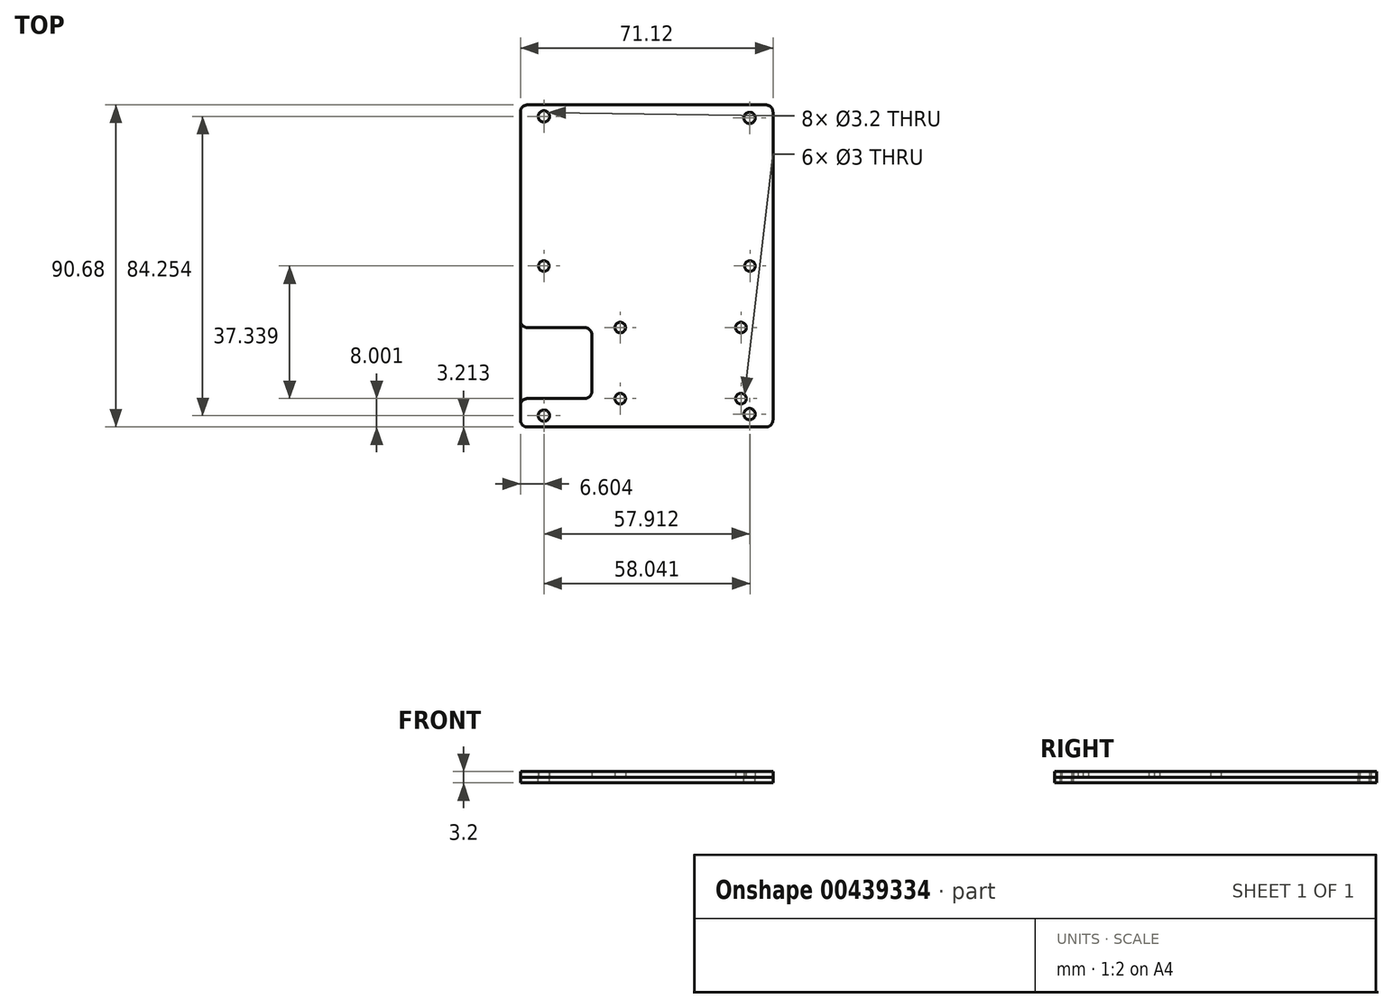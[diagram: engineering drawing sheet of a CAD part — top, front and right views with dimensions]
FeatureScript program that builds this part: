
annotation { "Feature Type Name" : "Feature", "Feature Type Description" : "" }
export const myFeature = defineFeature(function(context is Context, id is Id, definition is map)
    precondition{}
    {
        {
            var Q0;
            Q0=qCreatedBy(makeId("Top.planeOp"),FACE);
            var sketch = newSketch(context, id + "F0", { "sketchPlane" : qUnion([Q0])});
            skLineSegment(sketch, "E0.bottom", {"start": v(35.56, -55.5) * mm, "end": v(-35.56, -55.5) * mm});
            skLineSegment(sketch, "E0.top", {"start": v(35.56, 55.5) * mm, "end": v(-35.56, 55.5) * mm});
            skLineSegment(sketch, "E0.left", {"start": v(35.56, -55.5) * mm, "end": v(35.56, 55.5) * mm});
            skLineSegment(sketch, "E0.right", {"start": v(-35.56, -55.5) * mm, "end": v(-35.56, 55.5) * mm});
            skPoint(sketch, "E0.middle", {"position": v(0, 0) * mm});
            skCircle(sketch, "E1", {"center": v(-28.96, 42.13) * mm, "radius": 1.6 * mm});
            skCircle(sketch, "E2", {"center": v(28.96, 41.7) * mm, "radius": 1.6 * mm});
            skLineSegment(sketch, "E3", {"start": v(-75.95, 0) * mm, "end": v(69.97, 0) * mm, "construction": true});
            skLineSegment(sketch, "E4", {"start": v(0, -74.25) * mm, "end": v(0, 72.53) * mm, "construction": true});
            skLineSegment(sketch, "E5", {"start": v(-28.96, 42.13) * mm, "end": v(28.96, 41.7) * mm, "construction": true});
            skPoint(sketch, "E6", {"position": v(0, 41.91) * mm});
            skCircle(sketch, "E7.MirrorC", {"center": v(-28.96, -42.13) * mm, "radius": 1.6 * mm});
            skCircle(sketch, "E8.MirrorC", {"center": v(28.96, -41.7) * mm, "radius": 1.6 * mm});
            skLineSegment(sketch, "E9.bottom", {"start": v(35.56, 55.5) * mm, "end": v(16.5, 55.5) * mm});
            skLineSegment(sketch, "E9.top", {"start": v(35.56, 45.34) * mm, "end": v(22.86, 45.34) * mm});
            skLineSegment(sketch, "E9.left", {"start": v(35.56, 55.5) * mm, "end": v(35.56, 45.34) * mm});
            skLineSegment(sketch, "E9.right", {"start": v(16.5, 55.5) * mm, "end": v(16.5, 51.69) * mm});
            skPoint(sketch, "E10.visualSharp", {"position": v(16.5, 45.34) * mm});
            skArc(sketch, "E10.filletArc", {"start": v(16.5, 51.69) * mm, "mid": v(18.37, 47.2) * mm, "end": v(22.86, 45.34) * mm});
            skLineSegment(sketch, "E11.MirrorCS", {"start": v(-35.56, 45.34) * mm, "end": v(-22.86, 45.34) * mm});
            skPoint(sketch, "E12.MirrorP", {"position": v(-16.5, 45.34) * mm});
            skArc(sketch, "E13.MirrorCS", {"start": v(-16.5, 51.69) * mm, "mid": v(-18.37, 47.2) * mm, "end": v(-22.86, 45.34) * mm});
            skLineSegment(sketch, "E14.MirrorCS", {"start": v(-16.5, 55.5) * mm, "end": v(-16.5, 51.69) * mm});
            skLineSegment(sketch, "E15.MirrorCS", {"start": v(35.56, -45.34) * mm, "end": v(22.86, -45.34) * mm});
            skArc(sketch, "E16.MirrorCS", {"start": v(16.5, -51.69) * mm, "mid": v(18.37, -47.2) * mm, "end": v(22.86, -45.34) * mm});
            skLineSegment(sketch, "E17.MirrorCS", {"start": v(16.5, -55.5) * mm, "end": v(16.5, -51.69) * mm});
            skLineSegment(sketch, "E18.MirrorCS", {"start": v(-16.5, -55.5) * mm, "end": v(-16.5, -51.69) * mm});
            skArc(sketch, "E19.MirrorCS", {"start": v(-16.5, -51.69) * mm, "mid": v(-18.37, -47.2) * mm, "end": v(-22.86, -45.34) * mm});
            skLineSegment(sketch, "E20.MirrorCS", {"start": v(-35.56, -45.34) * mm, "end": v(-22.86, -45.34) * mm});
            skLineSegment(sketch, "E21", {"start": v(28.96, 41.7) * mm, "end": v(28.96, -41.7) * mm, "construction": true});
            skPoint(sketch, "E22", {"position": v(28.96, 0) * mm});
            skLineSegment(sketch, "E23", {"start": v(22.86, 45.34) * mm, "end": v(-22.86, 45.34) * mm});
            skLineSegment(sketch, "E24", {"start": v(22.86, -45.34) * mm, "end": v(-22.86, -45.34) * mm});
            skSolve(sketch);
        }
        {
            var Q0;
            Q0=makeQuery(id+"F0.imprint","IMPRINT",FACE,{"disambiguationData":[TD([[makeQuery(id+"F0.imprint","IMPRINT",EDGE,{"derivedFrom":sQuery(id+"F0.wireOp",EDGE,"E1")}),-1.0]])]});
            extrude(context, id + "F1", {"entities" : qUnion([Q0]), "depth" : -1.6 * mm});
        }
        {
            var Q0;
            Q0=makeQuery(id+"F1.opExtrude","SWEPT_EDGE",EDGE,{"disambiguationData":[OSD([sQuery(id+"F0.wireOp",EDGE,"E13.MirrorCS"),sQuery(id+"F0.wireOp",EDGE,"E14.MirrorCS"),sQuery(id+"F0.wireOp",EDGE,"XZWQAJ3d-1OIx-bhkB-XilU-HeP7hMm0Z5BM")])]});
            var Q1;
            Q1=makeQuery(id+"F1.opExtrude","SWEPT_EDGE",EDGE,{"disambiguationData":[OSD([sQuery(id+"F0.wireOp",EDGE,"E0.right"),sQuery(id+"F0.wireOp",EDGE,"E11.MirrorCS")])]});
            var Q2;
            Q2=makeQuery(id+"F1.opExtrude","SWEPT_EDGE",EDGE,{"disambiguationData":[OSD([sQuery(id+"F0.wireOp",EDGE,"E0.right"),sQuery(id+"F0.wireOp",EDGE,"uSXCYccX-oIT5-2jNX-9JdD-URnODkG6B3Dm")])]});
            var Q3;
            Q3=makeQuery(id+"F1.opExtrude","SWEPT_EDGE",EDGE,{"disambiguationData":[OSD([sQuery(id+"F0.wireOp",EDGE,"yg8D8cCT-qt1p-nqNG-vVnf-B0wRxMkFlv7V"),sQuery(id+"F0.wireOp",EDGE,"uSXCYccX-oIT5-2jNX-9JdD-URnODkG6B3Dm")])]});
            var Q4;
            Q4=makeQuery(id+"F1.opExtrude","SWEPT_EDGE",EDGE,{"disambiguationData":[OSD([sQuery(id+"F0.wireOp",EDGE,"E0.left"),sQuery(id+"F0.wireOp",EDGE,"yEekSQkt-yV80-caZB-sCm5-k8Zb9SgICgdF")])]});
            var Q5;
            Q5=makeQuery(id+"F1.opExtrude","SWEPT_EDGE",EDGE,{"disambiguationData":[OSD([sQuery(id+"F0.wireOp",EDGE,"E9.right"),sQuery(id+"F0.wireOp",EDGE,"E10.filletArc"),sQuery(id+"F0.wireOp",EDGE,"XZWQAJ3d-1OIx-bhkB-XilU-HeP7hMm0Z5BM")])]});
            var Q6;
            Q6=makeQuery(id+"F1.opExtrude","SWEPT_EDGE",EDGE,{"disambiguationData":[OSD([sQuery(id+"F0.wireOp",EDGE,"E0.left"),sQuery(id+"F0.wireOp",EDGE,"E9.top"),sQuery(id+"F0.wireOp",EDGE,"E9.left")])]});
            fillet(context, id + "F2", {"entities" : qUnion([Q0, Q1, Q2, Q3, Q4, Q5, Q6]), "radius" : 2 * mm, "tangentPropagation" : true, "allowEdgeOverflow" : false});
        }
        {
            var Q0;
            Q0=makeQuery(id+"F0.imprint","IMPRINT",FACE,{"disambiguationData":[TD([[makeQuery(id+"F0.imprint","IMPRINT",EDGE,{"derivedFrom":sQuery(id+"F0.wireOp",EDGE,"E1")}),-1.0]])]});
            var sketch = newSketch(context, id + "F3", { "sketchPlane" : qUnion([Q0])});
            skCircle(sketch, "E25", {"center": v(0, 17) * mm, "radius": 27.5 * mm});
            skLineSegment(sketch, "E26", {"start": v(0, 17) * mm, "end": v(-31.25, -37.13) * mm});
            skLineSegment(sketch, "E27.bottom", {"start": v(34.56, -17.34) * mm, "end": v(-15.44, -17.34) * mm});
            skLineSegment(sketch, "E27.top", {"start": v(34.56, -37.34) * mm, "end": v(-15.44, -37.34) * mm});
            skLineSegment(sketch, "E27.left", {"start": v(34.56, -17.34) * mm, "end": v(34.56, -37.34) * mm});
            skLineSegment(sketch, "E27.right", {"start": v(-15.44, -17.34) * mm, "end": v(-15.44, -37.34) * mm});
            skCircle(sketch, "E28", {"center": v(-7.44, -17.34) * mm, "radius": 1.5 * mm});
            skCircle(sketch, "E29", {"center": v(-7.44, -37.34) * mm, "radius": 1.5 * mm});
            skCircle(sketch, "E30", {"center": v(26.56, -17.34) * mm, "radius": 1.5 * mm});
            skCircle(sketch, "E31", {"center": v(26.56, -37.34) * mm, "radius": 1.5 * mm});
            skPoint(sketch, "E32", {"position": v(9.56, -17.34) * mm});
            skPoint(sketch, "E33", {"position": v(9.56, -37.34) * mm});
            skLineSegment(sketch, "E34.bottom", {"start": v(-15.44, -17.34) * mm, "end": v(-35.6, -17.34) * mm});
            skLineSegment(sketch, "E34.top", {"start": v(-15.44, -37.34) * mm, "end": v(-35.6, -37.34) * mm});
            skLineSegment(sketch, "E34.right", {"start": v(-35.6, -17.34) * mm, "end": v(-35.6, -37.34) * mm});
            skCircle(sketch, "E35", {"center": v(29.08, 0) * mm, "radius": 1.5 * mm});
            skCircle(sketch, "E36", {"center": v(-28.96, 0) * mm, "radius": 1.5 * mm});
            skLineSegment(sketch, "E37", {"start": v(-28.96, 0) * mm, "end": v(-28.96, 42.13) * mm});
            skLineSegment(sketch, "E38", {"start": v(-28.96, 17.02) * mm, "end": v(28.96, 17.02) * mm});
            skSolve(sketch);
        }
        {
            var Q0;
            {var subQ21=sQuery(id+"F3.wireOp",EDGE,"E27.left");Q0=makeQuery(id+"F3.imprint","IMPRINT",FACE,{"disambiguationData":[TD([[makeQuery(id+"F3.imprint","IMPRINT",EDGE,{"derivedFrom":subQ21}),1.0]])]});}
            var Q1;
            {var subQ4=sQuery(id+"F3.wireOp",EDGE,"E27.left");Q1=makeQuery(id+"F3.imprint","IMPRINT",FACE,{"disambiguationData":[TD([[makeQuery(id+"F3.imprint","IMPRINT",EDGE,{"derivedFrom":subQ4}),-1.0]])]});}
            var Q2;
            {var subQ0=sQuery(id+"F3.wireOp",EDGE,"E38");var subQ1=sQuery(id+"F3.wireOp",EDGE,"E25");var subQ2=makeQuery(id+"F3.imprint","INTERSECT",VERTEX,{"disambiguationData":[OD(0.0)],"derivedFrom":[subQ1,subQ0]});Q2=makeQuery(id+"F3.imprint","IMPRINT",FACE,{"disambiguationData":[TD([[makeQuery(id+"F3.imprint","IMPRINT",EDGE,{"disambiguationData":[TD([[subQ2,1.0]])],"derivedFrom":subQ1}),1.0]])]});}
            var Q3;
            {var subQ0=sQuery(id+"F3.wireOp",EDGE,"E25");var subQ1=makeQuery(id+"F3.imprint","IMPRINT",VERTEX,{"derivedFrom":subQ0});Q3=makeQuery(id+"F3.imprint","IMPRINT",FACE,{"disambiguationData":[TD([[makeQuery(id+"F3.imprint","IMPRINT",EDGE,{"disambiguationData":[TD([[subQ1,1.0]])],"derivedFrom":subQ0}),1.0]])]});}
            var Q4;
            Q4=sQuery(id+"F3.wireOp",EDGE,"E35");
            var Q5;
            Q5=sQuery(id+"F3.wireOp",EDGE,"E28");
            var Q6;
            Q6=sQuery(id+"F3.wireOp",EDGE,"E36");
            var Q7;
            Q7=sQuery(id+"F3.wireOp",EDGE,"E29");
            var Q8;
            Q8=sQuery(id+"F3.wireOp",EDGE,"E31");
            var Q9;
            Q9=sQuery(id+"F3.wireOp",EDGE,"E30");
            extrude(context, id + "F4", {"entities" : qUnion([Q0, Q1, Q2, Q3]), "surfaceEntities" : qUnion([Q4, Q5, Q6, Q7, Q8, Q9]), "depth" : 1.6 * mm});
        }
        {
            var Q0;
            Q0=makeQuery(id+"F4.opExtrude","SWEPT_EDGE",EDGE,{"disambiguationData":[OSD([sQuery(id+"F3.wireOp",EDGE,"E27.bottom"),sQuery(id+"F3.wireOp",EDGE,"E34.bottom"),sQuery(id+"F3.wireOp",EDGE,"E27.right")])]});
            var Q1;
            Q1=makeQuery(id+"F4.opExtrude","SWEPT_EDGE",EDGE,{"disambiguationData":[OSD([sQuery(id+"F0.wireOp",EDGE,"E0.right"),sQuery(id+"F3.wireOp",EDGE,"E34.bottom")])]});
            var Q2;
            Q2=makeQuery(id+"F4.opExtrude","SWEPT_EDGE",EDGE,{"disambiguationData":[OSD([sQuery(id+"F0.wireOp",EDGE,"E0.right"),sQuery(id+"F3.wireOp",EDGE,"E34.top")])]});
            var Q3;
            Q3=makeQuery(id+"F4.opExtrude","SWEPT_EDGE",EDGE,{"disambiguationData":[OSD([sQuery(id+"F3.wireOp",EDGE,"E27.top"),sQuery(id+"F3.wireOp",EDGE,"E34.top"),sQuery(id+"F3.wireOp",EDGE,"E27.right")])]});
            var Q4;
            Q4=makeQuery(id+"F4.opExtrude","SWEPT_EDGE",EDGE,{"disambiguationData":[OSD([sQuery(id+"F0.wireOp",EDGE,"E0.right"),sQuery(id+"F0.wireOp",EDGE,"E20.MirrorCS")])]});
            var Q5;
            Q5=makeQuery(id+"F4.opExtrude","SWEPT_EDGE",EDGE,{"disambiguationData":[OSD([sQuery(id+"F0.wireOp",EDGE,"E0.left"),sQuery(id+"F0.wireOp",EDGE,"E9.top")])]});
            var Q6;
            Q6=makeQuery(id+"F4.opExtrude","SWEPT_EDGE",EDGE,{"disambiguationData":[OSD([sQuery(id+"F0.wireOp",EDGE,"E0.right"),sQuery(id+"F0.wireOp",EDGE,"E11.MirrorCS")])]});
            var Q7;
            Q7=makeQuery(id+"F4.opExtrude","SWEPT_EDGE",EDGE,{"disambiguationData":[OSD([sQuery(id+"F0.wireOp",EDGE,"E0.left"),sQuery(id+"F0.wireOp",EDGE,"E15.MirrorCS")])]});
            fillet(context, id + "F5", {"entities" : qUnion([Q0, Q1, Q2, Q3, Q4, Q5, Q6, Q7]), "radius" : 2 * mm, "tangentPropagation" : true, "allowEdgeOverflow" : false});
        }
    });
